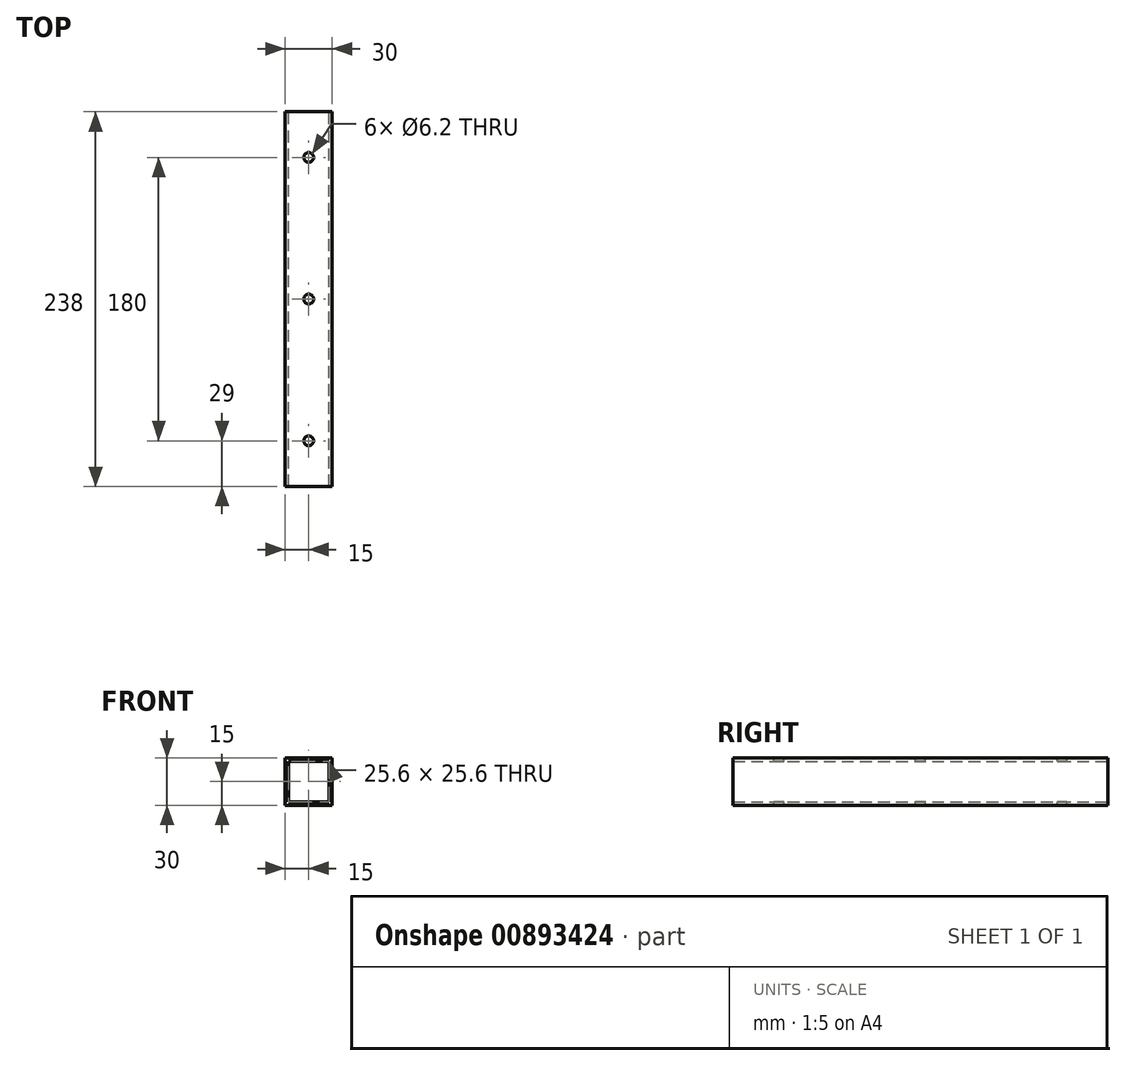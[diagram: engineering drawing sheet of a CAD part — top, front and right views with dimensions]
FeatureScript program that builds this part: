
annotation { "Feature Type Name" : "Feature", "Feature Type Description" : "" }
export const myFeature = defineFeature(function(context is Context, id is Id, definition is map)
    precondition{}
    {
        {
            var Q0;
            Q0=qCreatedBy(makeId("Front.planeOp"),FACE);
            var sketch = newSketch(context, id + "F0", { "sketchPlane" : qUnion([Q0])});
            skLineSegment(sketch, "E0.bottom", {"start": v(0, 0) * mm, "end": v(30, 0) * mm});
            skLineSegment(sketch, "E0.top", {"start": v(0, 30) * mm, "end": v(30, 30) * mm});
            skLineSegment(sketch, "E0.left", {"start": v(0, 0) * mm, "end": v(0, 30) * mm});
            skLineSegment(sketch, "E0.right", {"start": v(30, 0) * mm, "end": v(30, 30) * mm});
            skLineSegment(sketch, "E1.bottom", {"start": v(2.2, 27.8) * mm, "end": v(27.8, 27.8) * mm});
            skLineSegment(sketch, "E1.top", {"start": v(2.2, 2.2) * mm, "end": v(27.8, 2.2) * mm});
            skLineSegment(sketch, "E1.left", {"start": v(2.2, 27.8) * mm, "end": v(2.2, 2.2) * mm});
            skLineSegment(sketch, "E1.right", {"start": v(27.8, 27.8) * mm, "end": v(27.8, 2.2) * mm});
            skSolve(sketch);
        }
        {
            var Q0;
            Q0=makeQuery(id+"F0.imprint","IMPRINT",FACE,{"disambiguationData":[TD([[makeQuery(id+"F0.imprint","IMPRINT",EDGE,{"derivedFrom":sQuery(id+"F0.wireOp",EDGE,"E0.bottom")}),1.0]])]});
            extrude(context, id + "F1", {"entities" : qUnion([Q0]), "depth" : 238 * mm, "offsetDistance" : 25 * mm});
        }
        {
            var Q0;
            Q0=makeQuery(id+"F1.opExtrude","SWEPT_FACE",FACE,{"disambiguationData":[OSD([sQuery(id+"F0.wireOp",EDGE,"E0.top")])]});
            var sketch = newSketch(context, id + "F2", { "sketchPlane" : qUnion([Q0])});
            skCircle(sketch, "E2", {"center": v(15, -29) * mm, "radius": 3.1 * mm});
            skPoint(sketch, "E2.centerSnap0", {"position": v(15, 0) * mm});
            skCircle(sketch, "E3", {"center": v(15, -209) * mm, "radius": 3.1 * mm});
            skPoint(sketch, "E3.centerSnap0", {"position": v(15, -238) * mm});
            skCircle(sketch, "E4", {"center": v(15, -119) * mm, "radius": 3.1 * mm});
            skSolve(sketch);
        }
        {
            var Q0;
            Q0=makeQuery(id+"F2.imprint","IMPRINT",FACE,{"disambiguationData":[TD([[makeQuery(id+"F2.imprint","IMPRINT",EDGE,{"derivedFrom":sQuery(id+"F2.wireOp",EDGE,"E2")}),1.0]])]});
            var Q1;
            Q1=makeQuery(id+"F2.imprint","IMPRINT",FACE,{"disambiguationData":[TD([[makeQuery(id+"F2.imprint","IMPRINT",EDGE,{"derivedFrom":sQuery(id+"F2.wireOp",EDGE,"E4")}),1.0]])]});
            var Q2;
            Q2=makeQuery(id+"F2.imprint","IMPRINT",FACE,{"disambiguationData":[TD([[makeQuery(id+"F2.imprint","IMPRINT",EDGE,{"derivedFrom":sQuery(id+"F2.wireOp",EDGE,"E3")}),1.0]])]});
            extrude(context, id + "F3", {"entities" : qUnion([Q0, Q1, Q2]), "operationType" : NewBodyOperationType.REMOVE, "oppositeDirection" : true, "depth" : 35 * mm, "offsetDistance" : 25 * mm});
        }
    });
